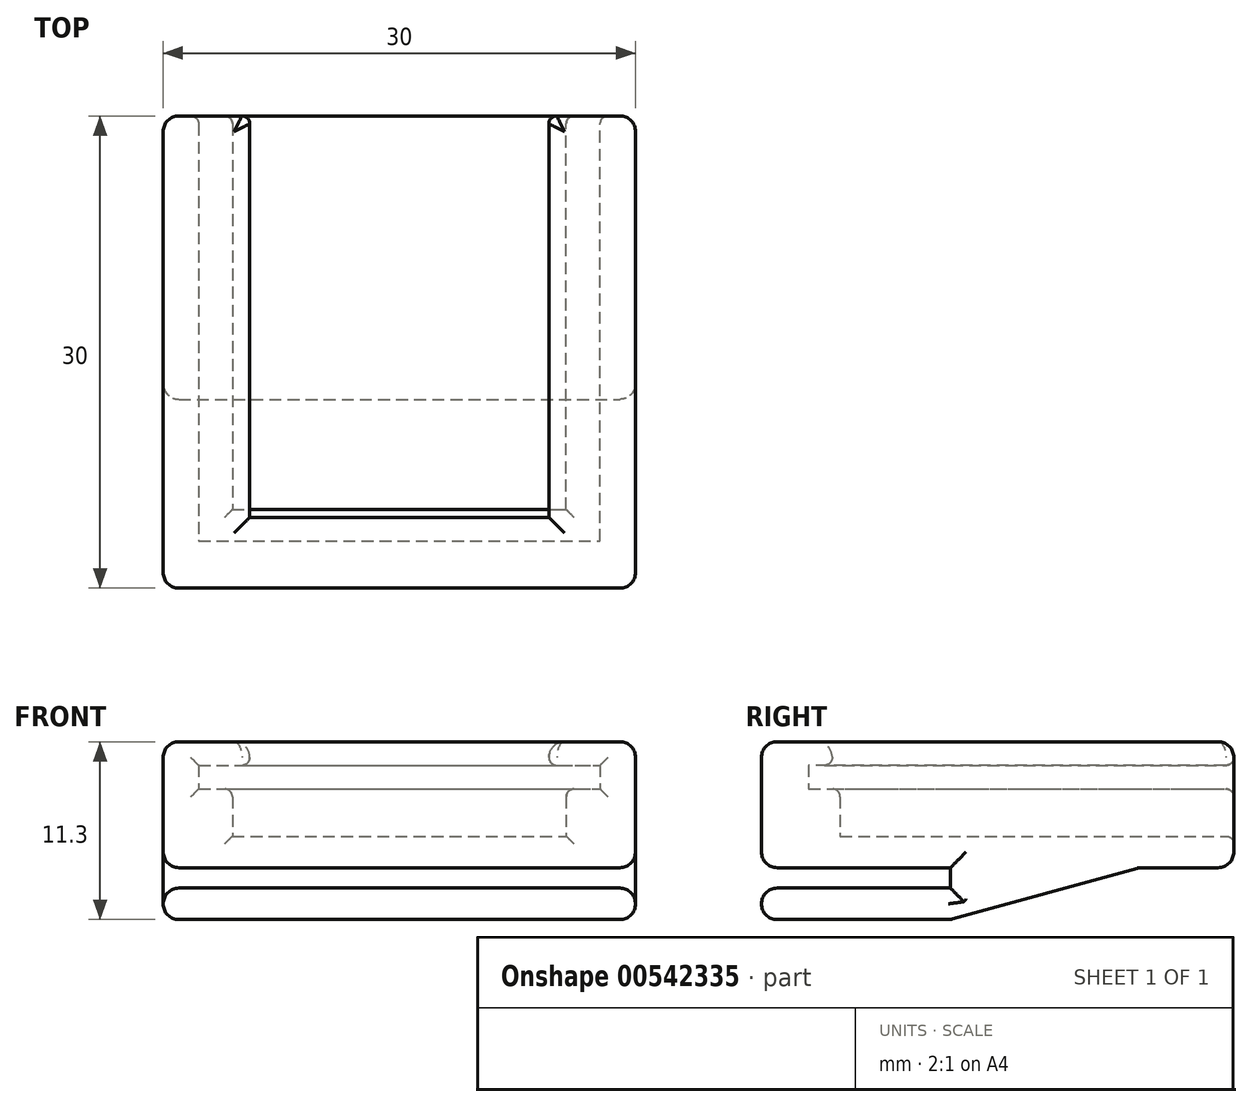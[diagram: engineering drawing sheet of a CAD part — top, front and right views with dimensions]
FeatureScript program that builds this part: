
annotation { "Feature Type Name" : "Feature", "Feature Type Description" : "" }
export const myFeature = defineFeature(function(context is Context, id is Id, definition is map)
    precondition{}
    {
        {
            var Q0;
            Q0=qCreatedBy(makeId("Top.planeOp"),FACE);
            var sketch = newSketch(context, id + "F0", { "sketchPlane" : qUnion([Q0])});
            skLineSegment(sketch, "E0.bottom", {"start": v(-15, 15) * mm, "end": v(15, 15) * mm});
            skLineSegment(sketch, "E0.top", {"start": v(-15, -15) * mm, "end": v(15, -15) * mm});
            skLineSegment(sketch, "E0.left", {"start": v(-15, 15) * mm, "end": v(-15, -15) * mm});
            skLineSegment(sketch, "E0.right", {"start": v(15, 15) * mm, "end": v(15, -15) * mm});
            skSolve(sketch);
        }
        {
            var Q0;
            Q0 = qSketchRegion(id + "F0", true);
            extrude(context, id + "F1", {"entities" : qUnion([Q0]), "depth" : 2 * mm, "offsetDistance" : 25 * mm});
        }
        {
            var Q0;
            Q0=makeQuery(id+"F1.opExtrude","CAP_FACE",FACE,{"disambiguationData":[OSD([sQuery(id+"F0.wireOp",EDGE,"E0.bottom"),sQuery(id+"F0.wireOp",EDGE,"E0.top"),sQuery(id+"F0.wireOp",EDGE,"E0.left"),sQuery(id+"F0.wireOp",EDGE,"E0.right")])],"isStart":false});
            var sketch = newSketch(context, id + "F2", { "sketchPlane" : qUnion([Q0])});
            skLineSegment(sketch, "E1", {"start": v(-15, 15) * mm, "end": v(-10.6, 15) * mm});
            skLineSegment(sketch, "E2", {"start": v(-15, -15) * mm, "end": v(-15, 15) * mm});
            skLineSegment(sketch, "E3", {"start": v(15, -15) * mm, "end": v(15, 15) * mm});
            skLineSegment(sketch, "E4", {"start": v(15, 15) * mm, "end": v(10.6, 15) * mm});
            skLineSegment(sketch, "E5", {"start": v(-10.6, 15) * mm, "end": v(-10.6, -10) * mm});
            skLineSegment(sketch, "E6", {"start": v(-10.6, -10) * mm, "end": v(10.6, -10) * mm});
            skLineSegment(sketch, "E7", {"start": v(10.6, -10) * mm, "end": v(10.6, 15) * mm});
            skLineSegment(sketch, "E8", {"start": v(-15, -15) * mm, "end": v(15, -15) * mm});
            skSolve(sketch);
        }
        {
            var Q0;
            Q0 = qSketchRegion(id + "F2", true);
            extrude(context, id + "F3", {"entities" : qUnion([Q0]), "operationType" : NewBodyOperationType.ADD, "depth" : 3 * mm, "offsetDistance" : 25 * mm});
        }
        {
            var Q0;
            Q0=makeQuery(id+"F3.opExtrude","CAP_FACE",FACE,{"disambiguationData":[OSD([sQuery(id+"F2.wireOp",EDGE,"E1"),sQuery(id+"F2.wireOp",EDGE,"E2"),sQuery(id+"F2.wireOp",EDGE,"E3"),sQuery(id+"F2.wireOp",EDGE,"E4"),sQuery(id+"F2.wireOp",EDGE,"E5"),sQuery(id+"F2.wireOp",EDGE,"E6"),sQuery(id+"F2.wireOp",EDGE,"E7"),sQuery(id+"F2.wireOp",EDGE,"E8")])],"isStart":false});
            var sketch = newSketch(context, id + "F4", { "sketchPlane" : qUnion([Q0])});
            skLineSegment(sketch, "E9", {"start": v(-15, 15) * mm, "end": v(-12.75, 15) * mm});
            skLineSegment(sketch, "E10", {"start": v(-12.75, 15) * mm, "end": v(-12.75, -12) * mm});
            skLineSegment(sketch, "E11", {"start": v(-12.75, -12) * mm, "end": v(12.75, -12) * mm});
            skLineSegment(sketch, "E12", {"start": v(12.75, -12) * mm, "end": v(12.75, 15) * mm});
            skLineSegment(sketch, "E13", {"start": v(12.75, 15) * mm, "end": v(15, 15) * mm});
            skLineSegment(sketch, "E14", {"start": v(15, 15) * mm, "end": v(15, -15) * mm});
            skLineSegment(sketch, "E15", {"start": v(15, -15) * mm, "end": v(-15, -15) * mm});
            skLineSegment(sketch, "E16", {"start": v(-15, -15) * mm, "end": v(-15, 15) * mm});
            skSolve(sketch);
        }
        {
            var Q0;
            Q0 = qSketchRegion(id + "F4", true);
            extrude(context, id + "F5", {"entities" : qUnion([Q0]), "operationType" : NewBodyOperationType.ADD, "depth" : 1.5 * mm, "offsetDistance" : 25 * mm});
        }
        {
            var Q0;
            Q0=makeQuery(id+"F3.opExtrude","CAP_EDGE",EDGE,{"disambiguationData":[OSD([sQuery(id+"F2.wireOp",EDGE,"E5")])],"isStart":false});
            var Q1;
            Q1=makeQuery(id+"F3.opExtrude","CAP_EDGE",EDGE,{"disambiguationData":[OSD([sQuery(id+"F2.wireOp",EDGE,"E6")])],"isStart":false});
            var Q2;
            Q2=makeQuery(id+"F3.opExtrude","CAP_EDGE",EDGE,{"disambiguationData":[OSD([sQuery(id+"F2.wireOp",EDGE,"E7")])],"isStart":false});
            var Q3;
            Q3=makeQuery(id+"F1.opExtrude","CAP_EDGE",EDGE,{"disambiguationData":[OSD([sQuery(id+"F0.wireOp",EDGE,"E0.bottom")])],"isStart":false});
            var Q4;
            Q4=makeQuery(id+"F3.opExtrude","SWEPT_EDGE",EDGE,{"disambiguationData":[OSD([sQuery(id+"F0.wireOp",EDGE,"E0.bottom"),sQuery(id+"F2.wireOp",EDGE,"E1"),sQuery(id+"F2.wireOp",EDGE,"E5")])]});
            var Q5;
            Q5=makeQuery(id+"F3.opExtrude","SWEPT_EDGE",EDGE,{"disambiguationData":[OSD([sQuery(id+"F0.wireOp",EDGE,"E0.bottom"),sQuery(id+"F2.wireOp",EDGE,"E4"),sQuery(id+"F2.wireOp",EDGE,"E7")])]});
            var Q6;
            Q6=makeQuery(id+"F3.opExtrude","CAP_EDGE",EDGE,{"disambiguationData":[OSD([sQuery(id+"F2.wireOp",EDGE,"E1")])],"isStart":false});
            var Q7;
            Q7=makeQuery(id+"F3.opExtrude","CAP_EDGE",EDGE,{"disambiguationData":[OSD([sQuery(id+"F2.wireOp",EDGE,"E4")])],"isStart":false});
            var Q8;
            Q8=makeQuery(id+"F5.opExtrude","SWEPT_EDGE",EDGE,{"disambiguationData":[OSD([sQuery(id+"F2.wireOp",EDGE,"E4"),sQuery(id+"F4.wireOp",EDGE,"E12"),sQuery(id+"F4.wireOp",EDGE,"E13")])]});
            var Q9;
            Q9=makeQuery(id+"F5.opExtrude","SWEPT_EDGE",EDGE,{"disambiguationData":[OSD([sQuery(id+"F2.wireOp",EDGE,"E1"),sQuery(id+"F4.wireOp",EDGE,"E9"),sQuery(id+"F4.wireOp",EDGE,"E10")])]});
            fillet(context, id + "F6", {"entities" : qUnion([Q0, Q1, Q2, Q3, Q4, Q5, Q6, Q7, Q8, Q9]), "radius" : 0.5 * mm, "tangentPropagation" : true, "allowEdgeOverflow" : false});
        }
        {
            var Q0;
            Q0=makeQuery(id+"F5.opExtrude","CAP_FACE",FACE,{"disambiguationData":[OSD([sQuery(id+"F4.wireOp",EDGE,"E9"),sQuery(id+"F4.wireOp",EDGE,"E10"),sQuery(id+"F4.wireOp",EDGE,"E11"),sQuery(id+"F4.wireOp",EDGE,"E12"),sQuery(id+"F4.wireOp",EDGE,"E13"),sQuery(id+"F4.wireOp",EDGE,"E14"),sQuery(id+"F4.wireOp",EDGE,"E15"),sQuery(id+"F4.wireOp",EDGE,"E16")])],"isStart":false});
            var sketch = newSketch(context, id + "F7", { "sketchPlane" : qUnion([Q0])});
            skLineSegment(sketch, "E17", {"start": v(-15, 15) * mm, "end": v(-9.5, 15) * mm});
            skLineSegment(sketch, "E18", {"start": v(-9.5, 15) * mm, "end": v(-9.5, -10.5) * mm});
            skLineSegment(sketch, "E19", {"start": v(-9.5, -10.5) * mm, "end": v(9.5, -10.5) * mm});
            skLineSegment(sketch, "E20", {"start": v(9.5, -10.5) * mm, "end": v(9.5, 15) * mm});
            skLineSegment(sketch, "E21", {"start": v(9.5, 15) * mm, "end": v(15, 15) * mm});
            skLineSegment(sketch, "E22", {"start": v(15, 15) * mm, "end": v(15, -15) * mm});
            skLineSegment(sketch, "E23", {"start": v(15, -15) * mm, "end": v(-15, -15) * mm});
            skLineSegment(sketch, "E24", {"start": v(-15, -15) * mm, "end": v(-15, 15) * mm});
            skSolve(sketch);
        }
        {
            var Q0;
            Q0 = qSketchRegion(id + "F7", true);
            extrude(context, id + "F8", {"entities" : qUnion([Q0]), "operationType" : NewBodyOperationType.ADD, "depth" : 1.5 * mm, "offsetDistance" : 25 * mm});
        }
        {
            var Q0;
            Q0=makeQuery(id+"F8.opExtrude","CAP_EDGE",EDGE,{"disambiguationData":[OSD([sQuery(id+"F7.wireOp",EDGE,"E17")])],"isStart":true});
            var Q1;
            Q1=makeQuery(id+"F8.opExtrude","CAP_EDGE",EDGE,{"disambiguationData":[OSD([sQuery(id+"F7.wireOp",EDGE,"E18")])],"isStart":true});
            var Q2;
            Q2=makeQuery(id+"F8.opExtrude","CAP_EDGE",EDGE,{"disambiguationData":[OSD([sQuery(id+"F7.wireOp",EDGE,"E19")])],"isStart":true});
            var Q3;
            Q3=makeQuery(id+"F8.opExtrude","CAP_EDGE",EDGE,{"disambiguationData":[OSD([sQuery(id+"F7.wireOp",EDGE,"E20")])],"isStart":true});
            var Q4;
            Q4=makeQuery(id+"F8.opExtrude","CAP_EDGE",EDGE,{"disambiguationData":[OSD([sQuery(id+"F7.wireOp",EDGE,"E21")])],"isStart":true});
            var Q5;
            Q5=makeQuery(id+"F8.opExtrude","SWEPT_EDGE",EDGE,{"disambiguationData":[OSD([sQuery(id+"F7.wireOp",EDGE,"E17"),sQuery(id+"F7.wireOp",EDGE,"E18")])]});
            var Q6;
            Q6=makeQuery(id+"F8.opExtrude","SWEPT_EDGE",EDGE,{"disambiguationData":[OSD([sQuery(id+"F7.wireOp",EDGE,"E20"),sQuery(id+"F7.wireOp",EDGE,"E21")])]});
            fillet(context, id + "F9", {"entities" : qUnion([Q0, Q1, Q2, Q3, Q4, Q5, Q6]), "radius" : 0.5 * mm, "tangentPropagation" : true, "allowEdgeOverflow" : false});
        }
        {
            var Q0;
            Q0=makeQuery(id+"F8.boolean.opBoolean","MERGE",FACE,{"derivedFrom":[makeQuery(id+"F5.boolean.opBoolean","MERGE",FACE,{"derivedFrom":[makeQuery(id+"F3.boolean.opBoolean","MERGE",FACE,{"derivedFrom":[makeQuery(id+"F1.opExtrude","SWEPT_FACE",FACE,{"disambiguationData":[OSD([sQuery(id+"F0.wireOp",EDGE,"E0.right")])]}),makeQuery(id+"F3.opExtrude","SWEPT_FACE",FACE,{"disambiguationData":[OSD([sQuery(id+"F2.wireOp",EDGE,"E3")])]})]}),makeQuery(id+"F5.opExtrude","SWEPT_FACE",FACE,{"disambiguationData":[OSD([sQuery(id+"F4.wireOp",EDGE,"E14")])]})]}),makeQuery(id+"F8.opExtrude","SWEPT_FACE",FACE,{"disambiguationData":[OSD([sQuery(id+"F7.wireOp",EDGE,"E22")])]})]});
            var sketch = newSketch(context, id + "F10", { "sketchPlane" : qUnion([Q0])});
            skLineSegment(sketch, "E25", {"start": v(-3, 0) * mm, "end": v(-3, -1.3) * mm});
            skLineSegment(sketch, "E26", {"start": v(-3, -1.3) * mm, "end": v(-15, -1.3) * mm});
            skLineSegment(sketch, "E27", {"start": v(-15, -1.3) * mm, "end": v(-15, -3.3) * mm});
            skLineSegment(sketch, "E28", {"start": v(-15, -3.3) * mm, "end": v(-3, -3.3) * mm});
            skLineSegment(sketch, "E29", {"start": v(-3, -3.3) * mm, "end": v(9, 0) * mm});
            skLineSegment(sketch, "E30", {"start": v(-3, 0) * mm, "end": v(9, 0) * mm});
            skSolve(sketch);
        }
        {
            var Q0;
            Q0 = qSketchRegion(id + "F10", true);
            extrude(context, id + "F11", {"entities" : qUnion([Q0]), "oppositeDirection" : true, "depth" : 30 * mm, "offsetDistance" : 25 * mm});
        }
        {
            var Q0;
            Q0=makeQuery(id+"F1.opExtrude","SWEPT_BODY",BODY,{"disambiguationData":[OSD([sQuery(id+"F0.wireOp",EDGE,"E0.bottom"),sQuery(id+"F0.wireOp",EDGE,"E0.top"),sQuery(id+"F0.wireOp",EDGE,"E0.left"),sQuery(id+"F0.wireOp",EDGE,"E0.right")])]});
            var Q1;
            Q1=makeQuery(id+"F11.opExtrude","SWEPT_BODY",BODY,{"disambiguationData":[OSD([sQuery(id+"F10.wireOp",EDGE,"E25"),sQuery(id+"F10.wireOp",EDGE,"E26"),sQuery(id+"F10.wireOp",EDGE,"E27"),sQuery(id+"F10.wireOp",EDGE,"E28"),sQuery(id+"F10.wireOp",EDGE,"E29"),sQuery(id+"F10.wireOp",EDGE,"E30")])]});
            booleanBodies(context, id + "F12", {"operationType" : BooleanOperationType.UNION, "tools" : qUnion([Q0, Q1])});
        }
        {
            var Q0;
            Q0=makeQuery(id+"F8.opExtrude","CAP_FACE",FACE,{"disambiguationData":[OSD([sQuery(id+"F7.wireOp",EDGE,"E17"),sQuery(id+"F7.wireOp",EDGE,"E18"),sQuery(id+"F7.wireOp",EDGE,"E19"),sQuery(id+"F7.wireOp",EDGE,"E20"),sQuery(id+"F7.wireOp",EDGE,"E21"),sQuery(id+"F7.wireOp",EDGE,"E22"),sQuery(id+"F7.wireOp",EDGE,"E23"),sQuery(id+"F7.wireOp",EDGE,"E24")])],"isStart":false});
            var Q1;
            Q1=makeQuery(id+"F12.opBoolean","MERGE",FACE,{"derivedFrom":[makeQuery(id+"F8.boolean.opBoolean","MERGE",FACE,{"derivedFrom":[makeQuery(id+"F5.boolean.opBoolean","MERGE",FACE,{"derivedFrom":[makeQuery(id+"F3.boolean.opBoolean","MERGE",FACE,{"derivedFrom":[makeQuery(id+"F1.opExtrude","SWEPT_FACE",FACE,{"disambiguationData":[OSD([sQuery(id+"F0.wireOp",EDGE,"E0.right")])]}),makeQuery(id+"F3.opExtrude","SWEPT_FACE",FACE,{"disambiguationData":[OSD([sQuery(id+"F2.wireOp",EDGE,"E3")])]})]}),makeQuery(id+"F5.opExtrude","SWEPT_FACE",FACE,{"disambiguationData":[OSD([sQuery(id+"F4.wireOp",EDGE,"E14")])]})]}),makeQuery(id+"F8.opExtrude","SWEPT_FACE",FACE,{"disambiguationData":[OSD([sQuery(id+"F7.wireOp",EDGE,"E22")])]})]}),makeQuery(id+"F11.opExtrude","CAP_FACE",FACE,{"disambiguationData":[OSD([sQuery(id+"F10.wireOp",EDGE,"E25"),sQuery(id+"F10.wireOp",EDGE,"E26"),sQuery(id+"F10.wireOp",EDGE,"E27"),sQuery(id+"F10.wireOp",EDGE,"E28"),sQuery(id+"F10.wireOp",EDGE,"E29"),sQuery(id+"F10.wireOp",EDGE,"E30")])],"isStart":true})]});
            var Q2;
            Q2=makeQuery(id+"F12.opBoolean","MERGE",FACE,{"derivedFrom":[makeQuery(id+"F8.boolean.opBoolean","MERGE",FACE,{"derivedFrom":[makeQuery(id+"F5.boolean.opBoolean","MERGE",FACE,{"derivedFrom":[makeQuery(id+"F3.boolean.opBoolean","MERGE",FACE,{"derivedFrom":[makeQuery(id+"F1.opExtrude","SWEPT_FACE",FACE,{"disambiguationData":[OSD([sQuery(id+"F0.wireOp",EDGE,"E0.left")])]}),makeQuery(id+"F3.opExtrude","SWEPT_FACE",FACE,{"disambiguationData":[OSD([sQuery(id+"F2.wireOp",EDGE,"E2")])]})]}),makeQuery(id+"F5.opExtrude","SWEPT_FACE",FACE,{"disambiguationData":[OSD([sQuery(id+"F4.wireOp",EDGE,"E16")])]})]}),makeQuery(id+"F8.opExtrude","SWEPT_FACE",FACE,{"disambiguationData":[OSD([sQuery(id+"F7.wireOp",EDGE,"E24")])]})]}),makeQuery(id+"F11.opExtrude","CAP_FACE",FACE,{"disambiguationData":[OSD([sQuery(id+"F10.wireOp",EDGE,"E25"),sQuery(id+"F10.wireOp",EDGE,"E26"),sQuery(id+"F10.wireOp",EDGE,"E27"),sQuery(id+"F10.wireOp",EDGE,"E28"),sQuery(id+"F10.wireOp",EDGE,"E29"),sQuery(id+"F10.wireOp",EDGE,"E30")])],"isStart":false})]});
            var Q3;
            {var subQ6=sQuery(id+"F0.wireOp",EDGE,"E0.bottom");var subQ7=sQuery(id+"F0.wireOp",EDGE,"E0.right");var subQ8=sQuery(id+"F0.wireOp",EDGE,"E0.left");Q3=makeQuery(id+"F12.opBoolean","SPLIT",FACE,{"disambiguationData":[TD([makeQuery(id+"F1.opExtrude","SWEPT_FACE",FACE,{"disambiguationData":[OSD([subQ6])]})])],"derivedFrom":makeQuery(id+"F1.opExtrude","CAP_FACE",FACE,{"disambiguationData":[OSD([subQ6,sQuery(id+"F0.wireOp",EDGE,"E0.top"),subQ8,subQ7])],"isStart":true})});}
            var Q4;
            Q4=makeQuery(id+"F11.opExtrude","SWEPT_EDGE",EDGE,{"disambiguationData":[OSD([sQuery(id+"F10.wireOp",EDGE,"E28"),sQuery(id+"F10.wireOp",EDGE,"E29")])]});
            var Q5;
            Q5=makeQuery(id+"F11.opExtrude","SWEPT_EDGE",EDGE,{"disambiguationData":[OSD([sQuery(id+"F0.wireOp",EDGE,"E0.right"),sQuery(id+"F10.wireOp",EDGE,"E29"),sQuery(id+"F10.wireOp",EDGE,"E30")])]});
            var Q6;
            Q6=makeQuery(id+"F11.opExtrude","SWEPT_EDGE",EDGE,{"disambiguationData":[OSD([sQuery(id+"F10.wireOp",EDGE,"E27"),sQuery(id+"F10.wireOp",EDGE,"E28")])]});
            var Q7;
            Q7=makeQuery(id+"F11.opExtrude","SWEPT_EDGE",EDGE,{"disambiguationData":[OSD([sQuery(id+"F10.wireOp",EDGE,"E26"),sQuery(id+"F10.wireOp",EDGE,"E27")])]});
            var Q8;
            Q8=makeQuery(id+"F1.opExtrude","CAP_EDGE",EDGE,{"disambiguationData":[OSD([sQuery(id+"F0.wireOp",EDGE,"E0.top")])],"isStart":true});
            fillet(context, id + "F13", {"entities" : qUnion([Q0, Q1, Q2, Q3, Q4, Q5, Q6, Q7, Q8]), "radius" : 1 * mm, "tangentPropagation" : true, "allowEdgeOverflow" : false});
        }
    });
